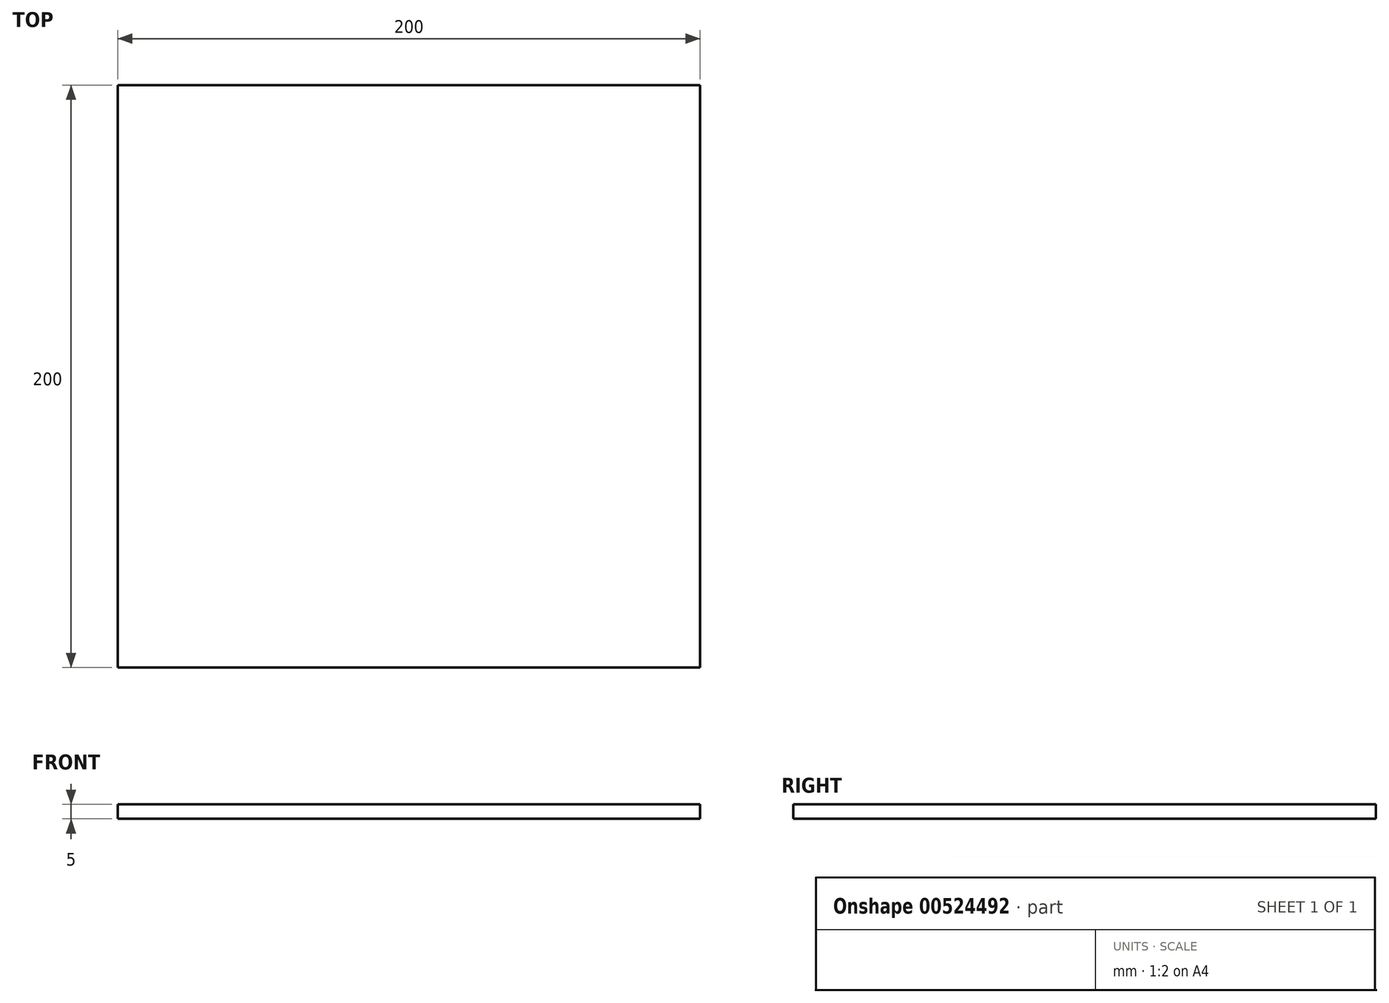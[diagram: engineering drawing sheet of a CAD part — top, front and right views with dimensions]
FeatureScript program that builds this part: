
annotation { "Feature Type Name" : "Feature", "Feature Type Description" : "" }
export const myFeature = defineFeature(function(context is Context, id is Id, definition is map)
    precondition{}
    {
        {
            assignVariable(context, id + "F0", {"name" : "baseThickness", "anyValue" : 5});
        }
        {
            var Q0;
            Q0=qCreatedBy(makeId("Top.planeOp"),FACE);
            var sketch = newSketch(context, id + "F1", { "sketchPlane" : qUnion([Q0])});
            skLineSegment(sketch, "E0.bottom", {"start": v(100, 100) * mm, "end": v(-100, 100) * mm});
            skLineSegment(sketch, "E0.top", {"start": v(100, -100) * mm, "end": v(-100, -100) * mm});
            skLineSegment(sketch, "E0.left", {"start": v(100, 100) * mm, "end": v(100, -100) * mm});
            skLineSegment(sketch, "E0.right", {"start": v(-100, 100) * mm, "end": v(-100, -100) * mm});
            skPoint(sketch, "E0.middle", {"position": v(0, 0) * mm});
            skSolve(sketch);
        }
        {
            var Q0;
            Q0 = qSketchRegion(id + "F1", true);
            extrude(context, id + "F2", {"entities" : qUnion([Q0]), "depth" : (getVariable(context, 'baseThickness')) * mm, "offsetDistance" : 25 * mm});
        }
    });
